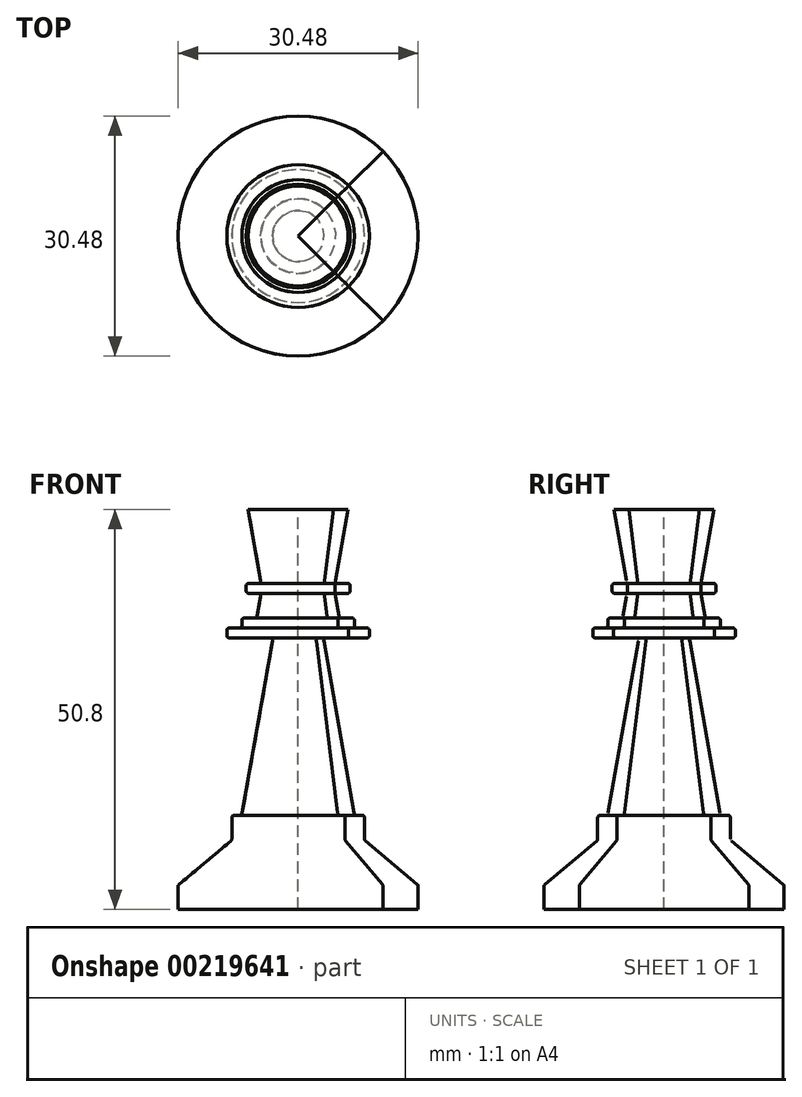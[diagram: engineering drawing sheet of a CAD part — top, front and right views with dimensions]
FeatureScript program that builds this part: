
annotation { "Feature Type Name" : "Feature", "Feature Type Description" : "" }
export const myFeature = defineFeature(function(context is Context, id is Id, definition is map)
    precondition{}
    {
        {
            var Q0;
            Q0=qCreatedBy(makeId("Front.planeOp"),FACE);
            var sketch = newSketch(context, id + "F0", { "sketchPlane" : qUnion([Q0])});
            skLineSegment(sketch, "E0.bottom", {"start": v(0, 0) * mm, "end": v(-15.24, 0) * mm});
            skLineSegment(sketch, "E0.top", {"start": v(0, 50.8) * mm, "end": v(-6.35, 50.8) * mm});
            skLineSegment(sketch, "E0.left", {"start": v(0, 0) * mm, "end": v(0, 50.8) * mm});
            skLineSegment(sketch, "E1", {"start": v(-15.24, 0) * mm, "end": v(-15.24, 2.93) * mm});
            skLineSegment(sketch, "E2", {"start": v(-15.13, 3.18) * mm, "end": v(-8.54, 8.7) * mm});
            skLineSegment(sketch, "E3", {"start": v(-8.43, 8.94) * mm, "end": v(-8.43, 11.65) * mm});
            skLineSegment(sketch, "E4", {"start": v(-8.11, 11.97) * mm, "end": v(-7.43, 11.97) * mm});
            skLineSegment(sketch, "E5", {"start": v(-7.11, 12.23) * mm, "end": v(-3.26, 34.11) * mm});
            skLineSegment(sketch, "E6", {"start": v(-3.57, 34.48) * mm, "end": v(-8.74, 34.48) * mm});
            skLineSegment(sketch, "E7", {"start": v(-9.06, 34.8) * mm, "end": v(-9.06, 35.44) * mm});
            skLineSegment(sketch, "E8", {"start": v(-8.74, 35.75) * mm, "end": v(-7.47, 35.75) * mm});
            skLineSegment(sketch, "E9", {"start": v(-7.15, 36.07) * mm, "end": v(-7.15, 36.7) * mm});
            skLineSegment(sketch, "E10", {"start": v(-6.83, 37.02) * mm, "end": v(-5.51, 37.02) * mm});
            skLineSegment(sketch, "E11", {"start": v(-5.2, 37.29) * mm, "end": v(-4.76, 39.78) * mm});
            skLineSegment(sketch, "E12", {"start": v(-5.07, 40.15) * mm, "end": v(-6.28, 40.15) * mm});
            skLineSegment(sketch, "E13", {"start": v(-6.6, 40.47) * mm, "end": v(-6.6, 41.1) * mm});
            skLineSegment(sketch, "E14", {"start": v(-6.28, 41.42) * mm, "end": v(-5.07, 41.42) * mm});
            skLineSegment(sketch, "E15", {"start": v(-4.76, 41.8) * mm, "end": v(-6.35, 50.8) * mm});
            skPoint(sketch, "E16.visualSharp", {"position": v(-15.24, 3.08) * mm});
            skArc(sketch, "E16.filletArc", {"start": v(-15.13, 3.18) * mm, "mid": v(-15.21, 3.07) * mm, "end": v(-15.24, 2.93) * mm});
            skPoint(sketch, "E17.visualSharp", {"position": v(-8.43, 8.8) * mm});
            skArc(sketch, "E17.filletArc", {"start": v(-8.54, 8.7) * mm, "mid": v(-8.46, 8.8) * mm, "end": v(-8.43, 8.94) * mm});
            skPoint(sketch, "E18.visualSharp", {"position": v(-3.2, 34.48) * mm});
            skArc(sketch, "E18.filletArc", {"start": v(-3.26, 34.11) * mm, "mid": v(-3.33, 34.37) * mm, "end": v(-3.57, 34.48) * mm});
            skPoint(sketch, "E19.visualSharp", {"position": v(-8.43, 11.97) * mm});
            skArc(sketch, "E19.filletArc", {"start": v(-8.11, 11.97) * mm, "mid": v(-8.34, 11.88) * mm, "end": v(-8.43, 11.65) * mm});
            skPoint(sketch, "E20.visualSharp", {"position": v(-7.16, 11.97) * mm});
            skArc(sketch, "E20.filletArc", {"start": v(-7.43, 11.97) * mm, "mid": v(-7.22, 12.04) * mm, "end": v(-7.11, 12.23) * mm});
            skPoint(sketch, "E21.visualSharp", {"position": v(-9.06, 34.48) * mm});
            skArc(sketch, "E21.filletArc", {"start": v(-9.06, 34.8) * mm, "mid": v(-8.96, 34.58) * mm, "end": v(-8.74, 34.48) * mm});
            skPoint(sketch, "E22.visualSharp", {"position": v(-9.06, 35.75) * mm});
            skArc(sketch, "E22.filletArc", {"start": v(-8.74, 35.75) * mm, "mid": v(-8.96, 35.66) * mm, "end": v(-9.06, 35.44) * mm});
            skPoint(sketch, "E23.visualSharp", {"position": v(-7.15, 35.75) * mm});
            skArc(sketch, "E23.filletArc", {"start": v(-7.47, 35.75) * mm, "mid": v(-7.25, 35.85) * mm, "end": v(-7.15, 36.07) * mm});
            skPoint(sketch, "E24.visualSharp", {"position": v(-7.15, 37.02) * mm});
            skArc(sketch, "E24.filletArc", {"start": v(-6.83, 37.02) * mm, "mid": v(-7.06, 36.93) * mm, "end": v(-7.15, 36.7) * mm});
            skPoint(sketch, "E25.visualSharp", {"position": v(-5.25, 37.02) * mm});
            skArc(sketch, "E25.filletArc", {"start": v(-5.51, 37.02) * mm, "mid": v(-5.3, 37.1) * mm, "end": v(-5.2, 37.29) * mm});
            skPoint(sketch, "E26.visualSharp", {"position": v(-4.7, 40.15) * mm});
            skArc(sketch, "E26.filletArc", {"start": v(-4.76, 39.78) * mm, "mid": v(-4.83, 40.04) * mm, "end": v(-5.07, 40.15) * mm});
            skPoint(sketch, "E27.visualSharp", {"position": v(-6.6, 40.15) * mm});
            skArc(sketch, "E27.filletArc", {"start": v(-6.6, 40.47) * mm, "mid": v(-6.5, 40.24) * mm, "end": v(-6.28, 40.15) * mm});
            skPoint(sketch, "E28.visualSharp", {"position": v(-6.6, 41.42) * mm});
            skArc(sketch, "E28.filletArc", {"start": v(-6.28, 41.42) * mm, "mid": v(-6.5, 41.33) * mm, "end": v(-6.6, 41.1) * mm});
            skPoint(sketch, "E29.visualSharp", {"position": v(-4.7, 41.42) * mm});
            skArc(sketch, "E29.filletArc", {"start": v(-5.07, 41.42) * mm, "mid": v(-4.83, 41.53) * mm, "end": v(-4.76, 41.8) * mm});
            skSolve(sketch);
        }
        {
            var Q0;
            Q0=makeQuery(id+"F0.imprint","IMPRINT",FACE,{"disambiguationData":[TD([[makeQuery(id+"F0.imprint","IMPRINT",EDGE,{"derivedFrom":sQuery(id+"F0.wireOp",EDGE,"E0.bottom")}),-1.0]])]});
            var Q1;
            Q1=sQuery(id+"F0.wireOp",EDGE,"E0.left");
            revolve(context, id + "F1", {"entities" : qUnion([Q0]), "axis" : qUnion([Q1]), "revolveType" : RevolveType.SYMMETRIC, "angle" : 270 * degree});
        }
        {
            var Q0;
            Q0=makeQuery(id+"F0.imprint","IMPRINT",FACE,{"disambiguationData":[TD([[makeQuery(id+"F0.imprint","IMPRINT",EDGE,{"derivedFrom":sQuery(id+"F0.wireOp",EDGE,"E0.bottom")}),-1.0]])]});
            var Q1;
            Q1=sQuery(id+"F0.wireOp",EDGE,"E0.left");
            revolve(context, id + "F2", {"entities" : qUnion([Q0]), "axis" : qUnion([Q1]), "revolveType" : RevolveType.FULL});
        }
    });
